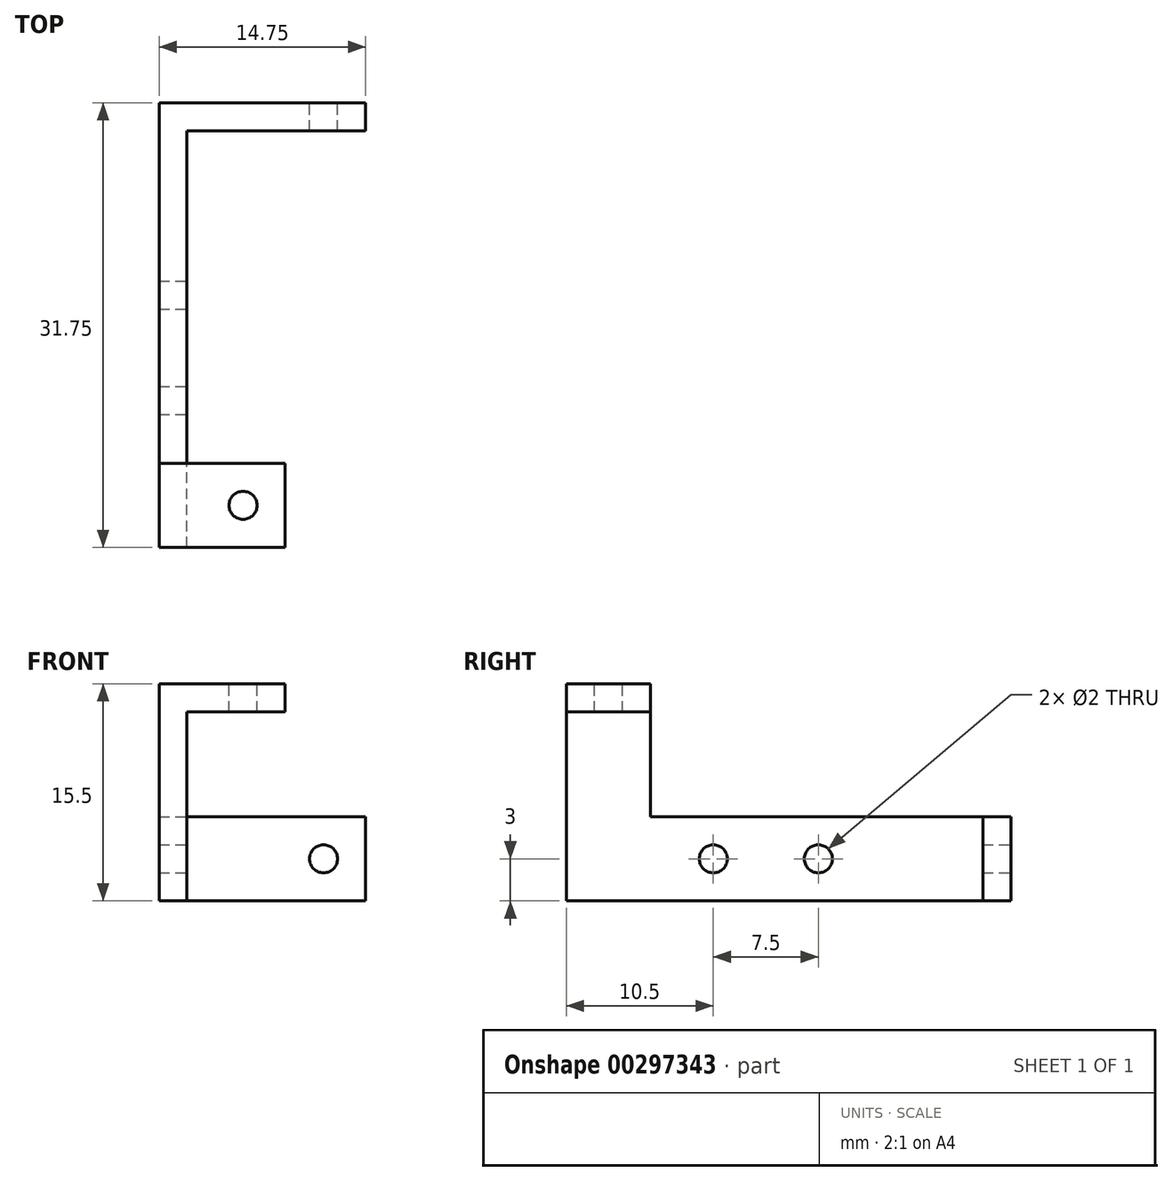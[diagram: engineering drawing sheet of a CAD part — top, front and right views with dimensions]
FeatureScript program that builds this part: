
annotation { "Feature Type Name" : "Feature", "Feature Type Description" : "" }
export const myFeature = defineFeature(function(context is Context, id is Id, definition is map)
    precondition{}
    {
        {
            var Q0;
            Q0=qCreatedBy(makeId("Front.planeOp"),FACE);
            var sketch = newSketch(context, id + "F0", { "sketchPlane" : qUnion([Q0])});
            skLineSegment(sketch, "E0.bottom", {"start": v(0, 0) * mm, "end": v(14.75, 0) * mm});
            skLineSegment(sketch, "E0.top", {"start": v(0, 6) * mm, "end": v(14.75, 6) * mm});
            skLineSegment(sketch, "E0.left", {"start": v(0, 0) * mm, "end": v(0, 6) * mm});
            skLineSegment(sketch, "E0.right", {"start": v(14.75, 0) * mm, "end": v(14.75, 6) * mm});
            skCircle(sketch, "E1", {"center": v(11.75, 3) * mm, "radius": 1 * mm});
            skSolve(sketch);
        }
        {
            var Q0;
            Q0=qSketchRegion(id+"F0",true);
            extrude(context, id + "F1", {"entities" : qUnion([Q0]), "depth" : 2 * mm});
        }
        {
            var Q0;
            Q0=makeQuery(id+"F1.opExtrude","CAP_FACE",FACE,{"disambiguationData":[OSD([sQuery(id+"F0.wireOp",EDGE,"E0.bottom"),sQuery(id+"F0.wireOp",EDGE,"E0.top"),sQuery(id+"F0.wireOp",EDGE,"E0.left"),sQuery(id+"F0.wireOp",EDGE,"E0.right"),sQuery(id+"F0.wireOp",EDGE,"E1")])],"isStart":false});
            var sketch = newSketch(context, id + "F2", { "sketchPlane" : qUnion([Q0])});
            skLineSegment(sketch, "E2.bottom", {"start": v(0, 0) * mm, "end": v(2, 0) * mm});
            skLineSegment(sketch, "E2.top", {"start": v(0, 6) * mm, "end": v(2, 6) * mm});
            skLineSegment(sketch, "E2.left", {"start": v(0, 0) * mm, "end": v(0, 6) * mm});
            skLineSegment(sketch, "E2.right", {"start": v(2, 0) * mm, "end": v(2, 6) * mm});
            skSolve(sketch);
        }
        {
            var Q0;
            Q0=qSketchRegion(id+"F2",true);
            extrude(context, id + "F3", {"entities" : qUnion([Q0]), "operationType" : NewBodyOperationType.ADD, "depth" : 14.75 * mm});
        }
        {
            var Q0;
            Q0=makeQuery(id+"F3.opExtrude","SWEPT_FACE",FACE,{"disambiguationData":[OSD([sQuery(id+"F2.wireOp",EDGE,"E2.right")])]});
            var sketch = newSketch(context, id + "F4", { "sketchPlane" : qUnion([Q0])});
            skCircle(sketch, "E3", {"center": v(-13.75, 3) * mm, "radius": 1 * mm});
            skSolve(sketch);
        }
        {
            var Q0;
            Q0=qSketchRegion(id+"F4",true);
            extrude(context, id + "F5", {"entities" : qUnion([Q0]), "operationType" : NewBodyOperationType.REMOVE, "oppositeDirection" : true, "depth" : 25 * mm});
        }
        {
            var Q0;
            Q0=makeQuery(id+"F3.opExtrude","CAP_FACE",FACE,{"disambiguationData":[OSD([sQuery(id+"F2.wireOp",EDGE,"E2.bottom"),sQuery(id+"F2.wireOp",EDGE,"E2.top"),sQuery(id+"F2.wireOp",EDGE,"E2.left"),sQuery(id+"F2.wireOp",EDGE,"E2.right")])],"isStart":false});
            var sketch = newSketch(context, id + "F6", { "sketchPlane" : qUnion([Q0])});
            skLineSegment(sketch, "E4.bottom", {"start": v(2, 6) * mm, "end": v(0, 6) * mm});
            skLineSegment(sketch, "E4.top", {"start": v(2, 0) * mm, "end": v(0, 0) * mm});
            skLineSegment(sketch, "E4.left", {"start": v(2, 6) * mm, "end": v(2, 0) * mm});
            skLineSegment(sketch, "E4.right", {"start": v(0, 6) * mm, "end": v(0, 0) * mm});
            skSolve(sketch);
        }
        {
            var Q0;
            Q0 = qSketchRegion(id + "F6", true);
            extrude(context, id + "F7", {"entities" : qUnion([Q0]), "operationType" : NewBodyOperationType.ADD, "depth" : 15 * mm});
        }
        {
            var Q0;
            Q0=makeQuery(id+"F7.boolean.opBoolean","MERGE",FACE,{"derivedFrom":[makeQuery(id+"F3.opExtrude","SWEPT_FACE",FACE,{"disambiguationData":[OSD([sQuery(id+"F2.wireOp",EDGE,"E2.right")])]}),makeQuery(id+"F7.opExtrude","SWEPT_FACE",FACE,{"disambiguationData":[OSD([sQuery(id+"F6.wireOp",EDGE,"E4.left")])]})]});
            var sketch = newSketch(context, id + "F8", { "sketchPlane" : qUnion([Q0])});
            skCircle(sketch, "E5", {"center": v(-21.25, 3) * mm, "radius": 1 * mm});
            skSolve(sketch);
        }
        {
            var Q0;
            Q0 = qSketchRegion(id + "F8", true);
            extrude(context, id + "F9", {"entities" : qUnion([Q0]), "operationType" : NewBodyOperationType.REMOVE, "oppositeDirection" : true, "depth" : 25 * mm});
        }
        {
            var Q0;
            Q0=makeQuery(id+"F7.boolean.opBoolean","MERGE",FACE,{"derivedFrom":[makeQuery(id+"F3.boolean.opBoolean","MERGE",FACE,{"derivedFrom":[makeQuery(id+"F1.opExtrude","SWEPT_FACE",FACE,{"disambiguationData":[OSD([sQuery(id+"F0.wireOp",EDGE,"E0.top")])]}),makeQuery(id+"F3.opExtrude","SWEPT_FACE",FACE,{"disambiguationData":[OSD([sQuery(id+"F2.wireOp",EDGE,"E2.top")])]})]}),makeQuery(id+"F7.opExtrude","SWEPT_FACE",FACE,{"disambiguationData":[OSD([sQuery(id+"F6.wireOp",EDGE,"E4.bottom")])]})]});
            var sketch = newSketch(context, id + "F10", { "sketchPlane" : qUnion([Q0])});
            skLineSegment(sketch, "E6.bottom", {"start": v(0, -31.75) * mm, "end": v(2, -31.75) * mm});
            skLineSegment(sketch, "E6.top", {"start": v(0, -25.75) * mm, "end": v(2, -25.75) * mm});
            skLineSegment(sketch, "E6.left", {"start": v(0, -31.75) * mm, "end": v(0, -25.75) * mm});
            skLineSegment(sketch, "E6.right", {"start": v(2, -31.75) * mm, "end": v(2, -25.75) * mm});
            skSolve(sketch);
        }
        {
            var Q0;
            Q0 = qSketchRegion(id + "F10", true);
            extrude(context, id + "F11", {"entities" : qUnion([Q0]), "operationType" : NewBodyOperationType.ADD, "depth" : 9.5 * mm});
        }
        {
            var Q0;
            Q0=makeQuery(id+"F11.boolean.opBoolean","MERGE",FACE,{"derivedFrom":[makeQuery(id+"F7.boolean.opBoolean","MERGE",FACE,{"derivedFrom":[makeQuery(id+"F3.opExtrude","SWEPT_FACE",FACE,{"disambiguationData":[OSD([sQuery(id+"F2.wireOp",EDGE,"E2.right")])]}),makeQuery(id+"F7.opExtrude","SWEPT_FACE",FACE,{"disambiguationData":[OSD([sQuery(id+"F6.wireOp",EDGE,"E4.left")])]})]}),makeQuery(id+"F11.opExtrude","SWEPT_FACE",FACE,{"disambiguationData":[OSD([sQuery(id+"F10.wireOp",EDGE,"E6.right")])]})]});
            var sketch = newSketch(context, id + "F12", { "sketchPlane" : qUnion([Q0])});
            skLineSegment(sketch, "E7.bottom", {"start": v(-31.75, 15.5) * mm, "end": v(-25.75, 15.5) * mm});
            skLineSegment(sketch, "E7.top", {"start": v(-31.75, 13.5) * mm, "end": v(-25.75, 13.5) * mm});
            skLineSegment(sketch, "E7.left", {"start": v(-31.75, 15.5) * mm, "end": v(-31.75, 13.5) * mm});
            skLineSegment(sketch, "E7.right", {"start": v(-25.75, 15.5) * mm, "end": v(-25.75, 13.5) * mm});
            skSolve(sketch);
        }
        {
            var Q0;
            Q0 = qSketchRegion(id + "F12", true);
            extrude(context, id + "F13", {"entities" : qUnion([Q0]), "operationType" : NewBodyOperationType.ADD, "depth" : 7 * mm});
        }
        {
            var Q0;
            Q0=makeQuery(id+"F13.boolean.opBoolean","MERGE",FACE,{"derivedFrom":[makeQuery(id+"F11.opExtrude","CAP_FACE",FACE,{"disambiguationData":[OSD([sQuery(id+"F10.wireOp",EDGE,"E6.bottom"),sQuery(id+"F10.wireOp",EDGE,"E6.top"),sQuery(id+"F10.wireOp",EDGE,"E6.left"),sQuery(id+"F10.wireOp",EDGE,"E6.right")])],"isStart":false}),makeQuery(id+"F13.opExtrude","SWEPT_FACE",FACE,{"disambiguationData":[OSD([sQuery(id+"F12.wireOp",EDGE,"E7.bottom")])]})]});
            var sketch = newSketch(context, id + "F14", { "sketchPlane" : qUnion([Q0])});
            skCircle(sketch, "E8", {"center": v(6, -28.75) * mm, "radius": 1 * mm});
            skSolve(sketch);
        }
        {
            var Q0;
            Q0 = qSketchRegion(id + "F14", true);
            extrude(context, id + "F15", {"entities" : qUnion([Q0]), "operationType" : NewBodyOperationType.REMOVE, "oppositeDirection" : true, "depth" : 25 * mm});
        }
    });
